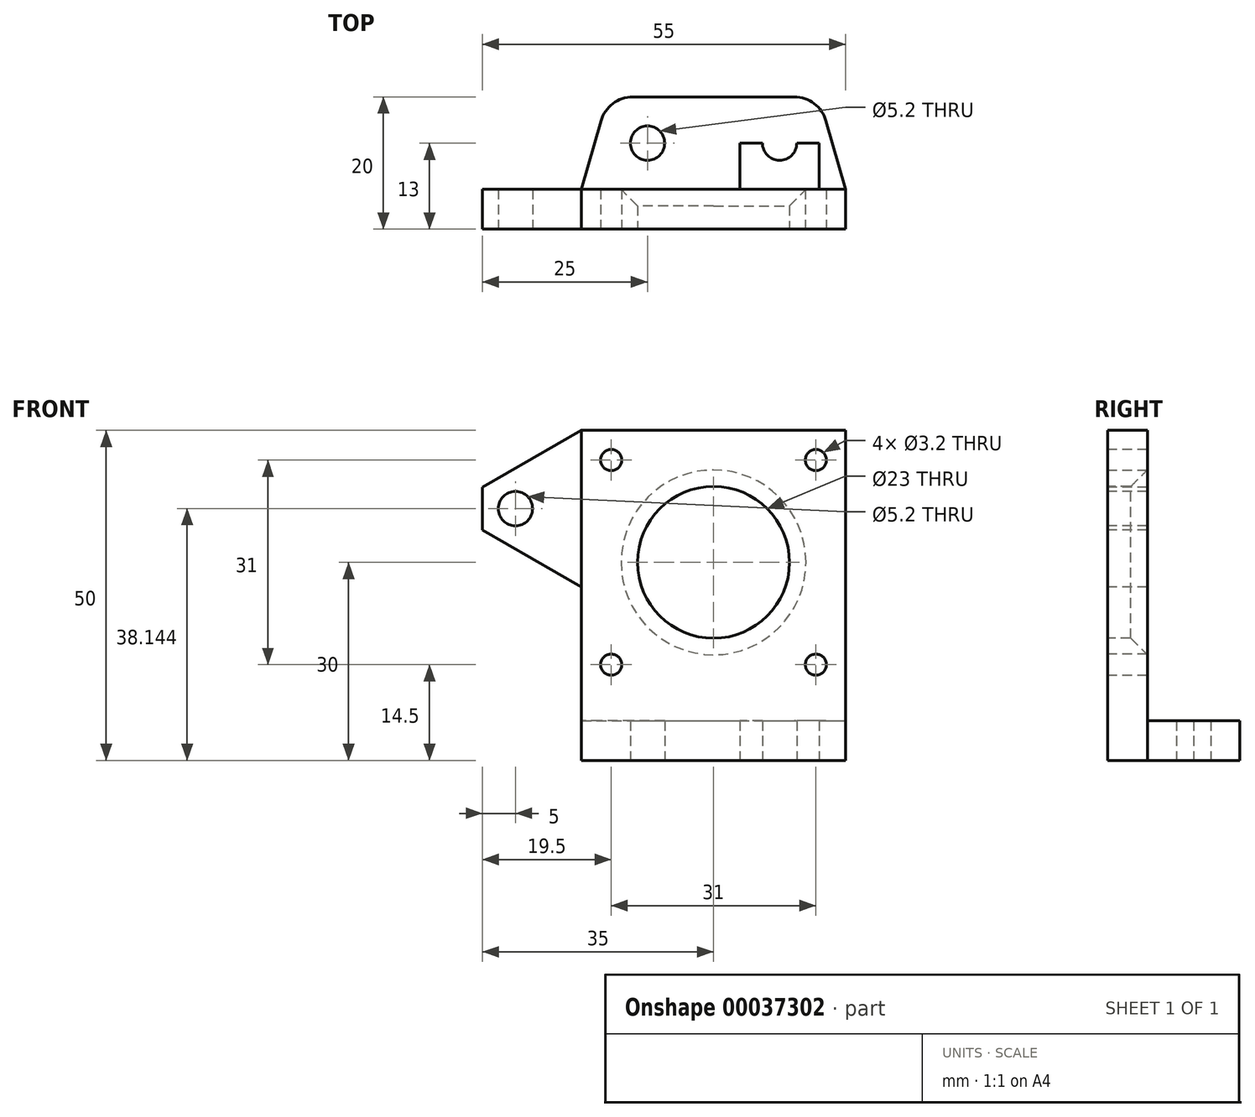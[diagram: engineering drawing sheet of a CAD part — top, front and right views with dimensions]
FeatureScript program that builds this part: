
annotation { "Feature Type Name" : "Feature", "Feature Type Description" : "" }
export const myFeature = defineFeature(function(context is Context, id is Id, definition is map)
    precondition{}
    {
        {
            assignVariable(context, id + "F0", {"name" : "defaultThickness", "anyValue" : 6 * mm});
        }
        {
            var Q0;
            Q0=qCreatedBy(makeId("Top.planeOp"),FACE);
            var sketch = newSketch(context, id + "F1", { "sketchPlane" : qUnion([Q0])});
            skLineSegment(sketch, "E0.rect.bottom", {"start": v(-20, 17.5) * mm, "end": v(20, 17.5) * mm});
            skLineSegment(sketch, "E0.rect.top", {"start": v(-20, 23.5) * mm, "end": v(20, 23.5) * mm});
            skLineSegment(sketch, "E0.rect.left", {"start": v(-20, 17.5) * mm, "end": v(-20, 23.5) * mm});
            skLineSegment(sketch, "E0.rect.right", {"start": v(20, 17.5) * mm, "end": v(20, 23.5) * mm});
            skPoint(sketch, "E0.rect.middle", {"position": v(0, 20.5) * mm});
            skLineSegment(sketch, "E1", {"start": v(-16, 23.5) * mm, "end": v(-16, 37.5) * mm});
            skLineSegment(sketch, "E2", {"start": v(-16, 37.5) * mm, "end": v(-4, 37.5) * mm});
            skLineSegment(sketch, "E3", {"start": v(-4, 37.5) * mm, "end": v(-4, 23.5) * mm});
            skLineSegment(sketch, "E4", {"start": v(-10, 37.5) * mm, "end": v(-10, 23.5) * mm, "construction": true});
            skLineSegment(sketch, "E5", {"start": v(-16, 30.5) * mm, "end": v(-4, 30.5) * mm, "construction": true});
            skPoint(sketch, "E6", {"position": v(-10, 30.5) * mm});
            skLineSegment(sketch, "E7", {"start": v(-16, 23.5) * mm, "end": v(-4, 23.5) * mm});
            skCircle(sketch, "E8", {"center": v(-10, 30.5) * mm, "radius": 2.6 * mm});
            skLineSegment(sketch, "E9.MirrorCS", {"start": v(16, 23.5) * mm, "end": v(4, 23.5) * mm});
            skPoint(sketch, "E10.MirrorP", {"position": v(10, 30.5) * mm});
            skLineSegment(sketch, "E11.MirrorCS", {"start": v(10, 37.5) * mm, "end": v(10, 23.5) * mm});
            skLineSegment(sketch, "E12.MirrorCS", {"start": v(16, 30.5) * mm, "end": v(4, 30.5) * mm});
            skCircle(sketch, "E13.MirrorC", {"center": v(10, 30.5) * mm, "radius": 2.6 * mm});
            skLineSegment(sketch, "E14.MirrorCS", {"start": v(4, 37.5) * mm, "end": v(4, 23.5) * mm});
            skLineSegment(sketch, "E15.MirrorCS", {"start": v(16, 37.5) * mm, "end": v(4, 37.5) * mm});
            skLineSegment(sketch, "E16.MirrorCS", {"start": v(16, 23.5) * mm, "end": v(16, 37.5) * mm});
            skLineSegment(sketch, "E17", {"start": v(-16, 37.5) * mm, "end": v(-20, 23.5) * mm});
            skLineSegment(sketch, "E18", {"start": v(16, 37.5) * mm, "end": v(20, 23.5) * mm});
            skLineSegment(sketch, "E19", {"start": v(-4, 37.5) * mm, "end": v(4, 37.5) * mm});
            skSolve(sketch);
        }
        {
            var Q0;
            Q0=makeQuery(id+"F1.imprint","IMPRINT",FACE,{"disambiguationData":[TD([[makeQuery(id+"F1.imprint","IMPRINT",EDGE,{"derivedFrom":sQuery(id+"F1.wireOp",EDGE,"E1")}),-1.0]])]});
            var Q1;
            {var subQ0=sQuery(id+"F1.wireOp",EDGE,"E15.MirrorCS");var subQ3=sQuery(id+"F1.wireOp",EDGE,"E11.MirrorCS");var subQ4=makeQuery(id+"F1.imprint","INTERSECT",VERTEX,{"derivedFrom":[subQ3,subQ0]});Q1=makeQuery(id+"F1.imprint","IMPRINT",FACE,{"disambiguationData":[TD([[makeQuery(id+"F1.imprint","IMPRINT",EDGE,{"disambiguationData":[TD([[subQ4,-1.0]])],"derivedFrom":subQ3}),-1.0]])]});}
            var Q2;
            {var subQ1=sQuery(id+"F1.wireOp",EDGE,"E15.MirrorCS");var subQ5=sQuery(id+"F1.wireOp",EDGE,"E11.MirrorCS");var subQ6=makeQuery(id+"F1.imprint","INTERSECT",VERTEX,{"derivedFrom":[subQ5,subQ1]});Q2=makeQuery(id+"F1.imprint","IMPRINT",FACE,{"disambiguationData":[TD([[makeQuery(id+"F1.imprint","IMPRINT",EDGE,{"disambiguationData":[TD([[subQ6,-1.0]])],"derivedFrom":subQ5}),1.0]])]});}
            var Q3;
            {var subQ3=sQuery(id+"F1.wireOp",EDGE,"E9.MirrorCS");var subQ7=sQuery(id+"F1.wireOp",EDGE,"E11.MirrorCS");var subQ9=makeQuery(id+"F1.imprint","INTERSECT",VERTEX,{"derivedFrom":[subQ3,subQ7]});Q3=makeQuery(id+"F1.imprint","IMPRINT",FACE,{"disambiguationData":[TD([[makeQuery(id+"F1.imprint","IMPRINT",EDGE,{"disambiguationData":[TD([[subQ9,1.0]])],"derivedFrom":subQ7}),1.0]])]});}
            var Q4;
            {var subQ3=sQuery(id+"F1.wireOp",EDGE,"E9.MirrorCS");var subQ7=sQuery(id+"F1.wireOp",EDGE,"E11.MirrorCS");var subQ9=makeQuery(id+"F1.imprint","INTERSECT",VERTEX,{"derivedFrom":[subQ3,subQ7]});Q4=makeQuery(id+"F1.imprint","IMPRINT",FACE,{"disambiguationData":[TD([[makeQuery(id+"F1.imprint","IMPRINT",EDGE,{"disambiguationData":[TD([[subQ9,1.0]])],"derivedFrom":subQ7}),-1.0]])]});}
            var Q5;
            {var subQ1=sQuery(id+"F1.wireOp",EDGE,"E1");Q5=makeQuery(id+"F1.imprint","IMPRINT",FACE,{"disambiguationData":[TD([[makeQuery(id+"F1.imprint","IMPRINT",EDGE,{"derivedFrom":subQ1}),1.0]])]});}
            var Q6;
            {var subQ5=sQuery(id+"F1.wireOp",EDGE,"E3");Q6=makeQuery(id+"F1.imprint","IMPRINT",FACE,{"disambiguationData":[TD([[makeQuery(id+"F1.imprint","IMPRINT",EDGE,{"derivedFrom":subQ5}),1.0]])]});}
            var Q7;
            {var subQ0=sQuery(id+"F1.wireOp",EDGE,"E18");Q7=makeQuery(id+"F1.imprint","IMPRINT",FACE,{"disambiguationData":[TD([[makeQuery(id+"F1.imprint","IMPRINT",EDGE,{"derivedFrom":subQ0}),-1.0]])]});}
            extrude(context, id + "F2", {"entities" : qUnion([Q0, Q1, Q2, Q3, Q4, Q5, Q6, Q7]), "depth" : getVariable(context, 'defaultThickness')});
        }
        {
            var Q0;
            Q0=makeQuery(id+"F1.imprint","IMPRINT",FACE,{"disambiguationData":[TD([[makeQuery(id+"F1.imprint","IMPRINT",EDGE,{"derivedFrom":sQuery(id+"F1.wireOp",EDGE,"E0.rect.bottom")}),1.0]])]});
            extrude(context, id + "F3", {"entities" : qUnion([Q0]), "depth" : 50 * mm});
        }
        {
            var Q0;
            Q0=makeQuery(id+"F3.opExtrude","SWEPT_FACE",FACE,{"disambiguationData":[OSD([sQuery(id+"F1.wireOp",EDGE,"E0.rect.bottom")])]});
            var sketch = newSketch(context, id + "F4", { "sketchPlane" : qUnion([Q0])});
            skLineSegment(sketch, "E20", {"start": v(0, 50) * mm, "end": v(0, 0) * mm, "construction": true});
            skLineSegment(sketch, "E21", {"start": v(-20, 30) * mm, "end": v(20, 30) * mm, "construction": true});
            skCircle(sketch, "E22", {"center": v(0, 30) * mm, "radius": 11.5 * mm});
            skCircle(sketch, "E23", {"center": v(-15.5, 45.5) * mm, "radius": 1.6 * mm});
            skCircle(sketch, "E24", {"center": v(-15.5, 14.5) * mm, "radius": 1.6 * mm});
            skCircle(sketch, "E25", {"center": v(15.5, 14.5) * mm, "radius": 1.6 * mm});
            skCircle(sketch, "E26", {"center": v(15.5, 45.5) * mm, "radius": 1.6 * mm});
            skSolve(sketch);
        }
        {
            var Q0;
            Q0=qSketchRegion(id+"F4",true);
            extrude(context, id + "F5", {"entities" : qUnion([Q0]), "operationType" : NewBodyOperationType.REMOVE, "endBound" : BoundingType.THROUGH_ALL, "oppositeDirection" : true, "depth" : 25 * mm});
        }
        {
            var Q0;
            Q0=makeQuery(id+"F3.opExtrude","SWEPT_FACE",FACE,{"disambiguationData":[OSD([sQuery(id+"F1.wireOp",EDGE,"E0.rect.bottom")])]});
            var sketch = newSketch(context, id + "F6", { "sketchPlane" : qUnion([Q0])});
            skLineSegment(sketch, "E27", {"start": v(-20, 41.4) * mm, "end": v(-35, 41.4) * mm});
            skLineSegment(sketch, "E28", {"start": v(-35, 41.4) * mm, "end": v(-35, 34.88) * mm});
            skLineSegment(sketch, "E29", {"start": v(-35, 34.88) * mm, "end": v(-20, 34.88) * mm});
            skPoint(sketch, "E30", {"position": v(-27.5, 41.4) * mm});
            skPoint(sketch, "E31", {"position": v(-27.5, 34.88) * mm});
            skPoint(sketch, "E32", {"position": v(-35, 38.14) * mm});
            skLineSegment(sketch, "E33", {"start": v(-20, 41.4) * mm, "end": v(-20, 34.88) * mm});
            skPoint(sketch, "E34", {"position": v(-20, 38.14) * mm});
            skLineSegment(sketch, "E35", {"start": v(-35, 38.14) * mm, "end": v(-20, 38.14) * mm, "construction": true});
            skCircle(sketch, "E36", {"center": v(-30, 38.14) * mm, "radius": 2.6 * mm, "construction": true});
            skLineSegment(sketch, "E37", {"start": v(-35, 41.4) * mm, "end": v(-20, 50) * mm});
            skLineSegment(sketch, "E38", {"start": v(-35, 34.88) * mm, "end": v(-20, 26.29) * mm});
            skLineSegment(sketch, "E39", {"start": v(-20, 50) * mm, "end": v(-20, 26.29) * mm});
            skLineSegment(sketch, "E40.MirrorCS", {"start": v(-20, 34.88) * mm, "end": v(-20, 41.4) * mm});
            skLineSegment(sketch, "E41.MirrorCS", {"start": v(-20, 34.88) * mm, "end": v(-35, 34.88) * mm});
            skLineSegment(sketch, "E42.MirrorCS", {"start": v(-35, 41.4) * mm, "end": v(-20, 41.4) * mm});
            skCircle(sketch, "E43.MirrorC", {"center": v(-30, 38.14) * mm, "radius": 2.6 * mm});
            skLineSegment(sketch, "E44.MirrorCS", {"start": v(-20, 26.29) * mm, "end": v(-20, 50) * mm});
            skLineSegment(sketch, "E45.MirrorCS", {"start": v(-35, 34.88) * mm, "end": v(-35, 41.4) * mm});
            skLineSegment(sketch, "E46", {"start": v(-20, 50) * mm, "end": v(-20, 41.4) * mm});
            skLineSegment(sketch, "E47", {"start": v(-20, 38.14) * mm, "end": v(-20, 34.88) * mm});
            skLineSegment(sketch, "E48.MirrorCS", {"start": v(-20, 38.14) * mm, "end": v(-20, 41.4) * mm});
            skLineSegment(sketch, "E49.MirrorCS", {"start": v(-20, 26.29) * mm, "end": v(-20, 34.88) * mm});
            skSolve(sketch);
        }
        {
            var Q0;
            Q0=qSketchRegion(id+"F6",true);
            extrude(context, id + "F7", {"entities" : qUnion([Q0]), "oppositeDirection" : true, "depth" : getVariable(context, 'defaultThickness')});
        }
        {
            var Q0;
            Q0=makeQuery(id+"F7.opExtrude","SWEPT_EDGE",EDGE,{"disambiguationData":[OSD([sQuery(id+"F6.wireOp",EDGE,"306b3cfc-551d-497d-8c43-a8ed09669cc44.MirrorCS"),sQuery(id+"F6.wireOp",EDGE,"306b3cfc-551d-497d-8c43-a8ed09669cc45.MirrorCS"),sQuery(id+"F6.wireOp",EDGE,"306b3cfc-551d-497d-8c43-a8ed09669cc410.MirrorCS")])]});
            var Q1;
            Q1=makeQuery(id+"F7.opExtrude","SWEPT_EDGE",EDGE,{"disambiguationData":[OSD([sQuery(id+"F6.wireOp",EDGE,"306b3cfc-551d-497d-8c43-a8ed09669cc46.MirrorCS"),sQuery(id+"F6.wireOp",EDGE,"306b3cfc-551d-497d-8c43-a8ed09669cc47.MirrorCS"),sQuery(id+"F6.wireOp",EDGE,"306b3cfc-551d-497d-8c43-a8ed09669cc410.MirrorCS")])]});
            var Q2;
            Q2=makeQuery(id+"F7.opExtrude","SWEPT_EDGE",EDGE,{"disambiguationData":[OSD([sQuery(id+"F6.wireOp",EDGE,"a75c6c92-6b33-47ab-839a-70fd0e169de0"),sQuery(id+"F6.wireOp",EDGE,"e9842276-5117-4aed-8551-042d3347c8a4"),sQuery(id+"F6.wireOp",EDGE,"1b59d14f-a3ec-4578-90db-0e0e2cb720d3")])]});
            var Q3;
            Q3=makeQuery(id+"F7.opExtrude","SWEPT_EDGE",EDGE,{"disambiguationData":[OSD([sQuery(id+"F6.wireOp",EDGE,"e1829bb6-4c8f-4a3e-b7cc-f9a1525636db"),sQuery(id+"F6.wireOp",EDGE,"a75c6c92-6b33-47ab-839a-70fd0e169de0"),sQuery(id+"F6.wireOp",EDGE,"f6659a32-1e39-4f74-95a5-c9b4f418ae41")])]});
            var Q4;
            Q4=makeQuery(id+"F2.opExtrude","SWEPT_EDGE",EDGE,{"disambiguationData":[OSD([sQuery(id+"F1.wireOp",EDGE,"E15.MirrorCS"),sQuery(id+"F1.wireOp",EDGE,"E16.MirrorCS"),sQuery(id+"F1.wireOp",EDGE,"E18")])]});
            var Q5;
            Q5=makeQuery(id+"F2.opExtrude","SWEPT_EDGE",EDGE,{"disambiguationData":[OSD([sQuery(id+"F1.wireOp",EDGE,"E1"),sQuery(id+"F1.wireOp",EDGE,"E2"),sQuery(id+"F1.wireOp",EDGE,"E17")])]});
            fillet(context, id + "F8", {"entities" : qUnion([Q0, Q1, Q2, Q3, Q4, Q5]), "radius" : 5 * mm, "tangentPropagation" : true, "allowEdgeOverflow" : false});
        }
        {
            var Q0;
            Q0=makeQuery(id+"F5.boolean.opBoolean","INTERSECT",EDGE,{"derivedFrom":[makeQuery(id+"F3.opExtrude","SWEPT_FACE",FACE,{"disambiguationData":[OSD([sQuery(id+"F1.wireOp",EDGE,"E0.rect.top"),sQuery(id+"F1.wireOp",EDGE,"E7"),sQuery(id+"F1.wireOp",EDGE,"E9.MirrorCS")])]}),makeQuery(id+"F5.opExtrude","SWEPT_FACE",FACE,{"disambiguationData":[OSD([sQuery(id+"F4.wireOp",EDGE,"E22")])]})]});
            chamfer(context, id + "F9", {"entities" : qUnion([Q0]), "width" : 2.5 * mm, "tangentPropagation" : true});
        }
    });
